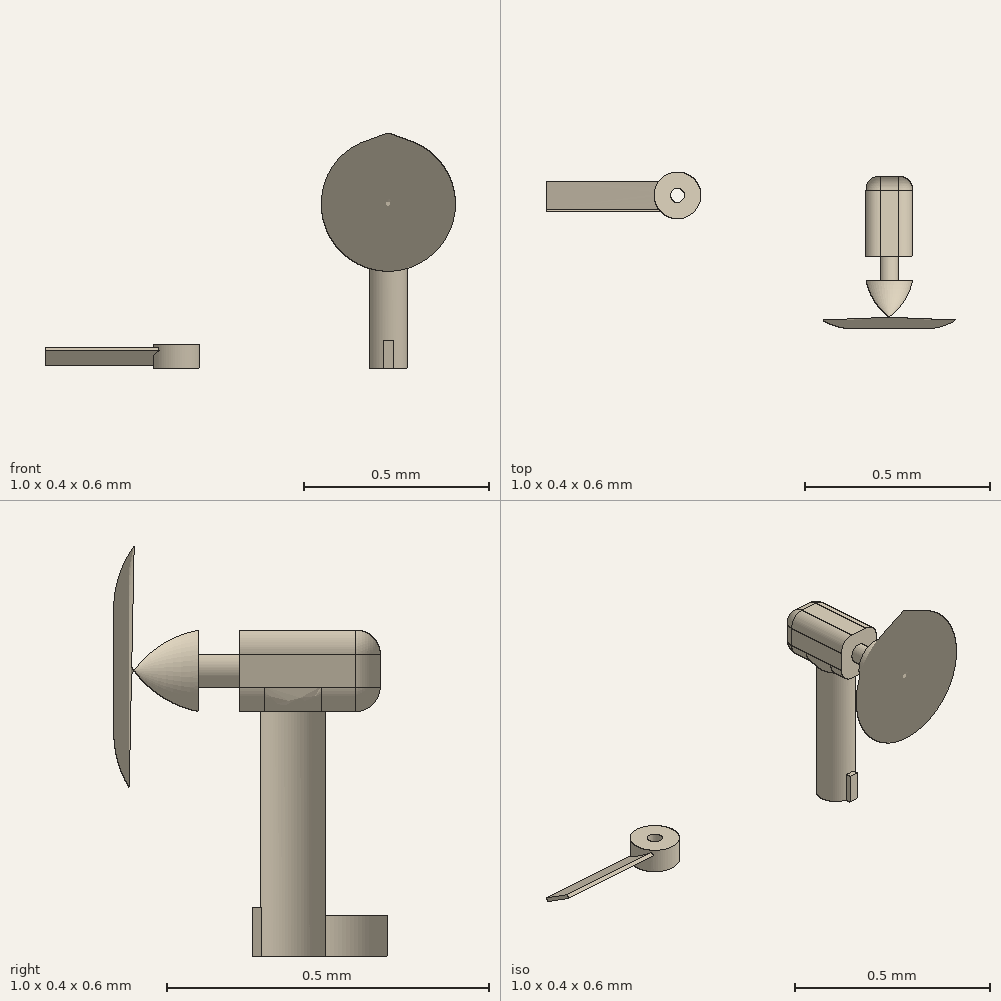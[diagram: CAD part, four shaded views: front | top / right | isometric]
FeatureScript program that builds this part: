
annotation { "Feature Type Name" : "Feature", "Feature Type Description" : "" }
export const myFeature = defineFeature(function(context is Context, id is Id, definition is map)
    precondition{}
    {
        {
            var Q0;
            Q0=qCreatedBy(makeId("Top.planeOp"),FACE);
            var sketch = newSketch(context, id + "F0", { "sketchPlane" : qUnion([Q0])});
            skCircle(sketch, "E0", {"center": v(0, 0) * mm, "radius": 0.05 * mm});
            skSolve(sketch);
        }
        {
            var Q0;
            Q0 = qSketchRegion(id + "F0", true);
            extrude(context, id + "F1", {"entities" : qUnion([Q0]), "depth" : 0.38 * mm});
        }
        {
            var Q0;
            Q0=makeQuery(id+"F1.opExtrude","CAP_FACE",FACE,{"disambiguationData":[OSD([sQuery(id+"F0.wireOp",EDGE,"E0")])],"isStart":false});
            var sketch = newSketch(context, id + "F2", { "sketchPlane" : qUnion([Q0])});
            skLineSegment(sketch, "E1.bottom", {"start": v(0.06, 0.14) * mm, "end": v(-0.06, 0.14) * mm});
            skLineSegment(sketch, "E1.left", {"start": v(0.06, 0.14) * mm, "end": v(0.06, -0.08) * mm});
            skLineSegment(sketch, "E1.right", {"start": v(-0.06, 0.14) * mm, "end": v(-0.06, -0.08) * mm});
            skPoint(sketch, "E1.middle", {"position": v(0, 0) * mm});
            skLineSegment(sketch, "E2", {"start": v(0.06, -0.08) * mm, "end": v(-0.06, -0.08) * mm});
            skPoint(sketch, "E1.top.end.orphan", {"position": v(-0.06, -0.14) * mm});
            skPoint(sketch, "E1.top.start.orphan", {"position": v(0.06, -0.14) * mm});
            skSolve(sketch);
        }
        {
            var Q0;
            Q0 = qSketchRegion(id + "F2", true);
            extrude(context, id + "F3", {"entities" : qUnion([Q0]), "operationType" : NewBodyOperationType.ADD, "depth" : 0.13 * mm});
        }
        {
            var Q0;
            Q0=makeQuery(id+"F3.opExtrude","CAP_EDGE",EDGE,{"disambiguationData":[OSD([sQuery(id+"F2.wireOp",EDGE,"E1.right")])],"isStart":false});
            var Q1;
            Q1=makeQuery(id+"F3.opExtrude","CAP_EDGE",EDGE,{"disambiguationData":[OSD([sQuery(id+"F2.wireOp",EDGE,"E1.right")])],"isStart":true});
            var Q2;
            Q2=makeQuery(id+"F3.opExtrude","CAP_EDGE",EDGE,{"disambiguationData":[OSD([sQuery(id+"F2.wireOp",EDGE,"E1.left")])],"isStart":true});
            var Q3;
            Q3=makeQuery(id+"F3.opExtrude","CAP_EDGE",EDGE,{"disambiguationData":[OSD([sQuery(id+"F2.wireOp",EDGE,"E1.left")])],"isStart":false});
            fillet(context, id + "F4", {"entities" : qUnion([Q0, Q1, Q2, Q3]), "radius" : 0.04 * mm, "tangentPropagation" : true, "allowEdgeOverflow" : false});
        }
        {
            var Q0;
            Q0=makeQuery(id+"F3.opExtrude","SWEPT_FACE",FACE,{"disambiguationData":[OSD([sQuery(id+"F2.wireOp",EDGE,"E2")])]});
            var sketch = newSketch(context, id + "F5", { "sketchPlane" : qUnion([Q0])});
            skLineSegment(sketch, "E3.0", {"start": v(0.03, 0.5) * mm, "end": v(-0.03, 0.5) * mm});
            skLineSegment(sketch, "E4.0", {"start": v(-0.06, 0.47) * mm, "end": v(-0.06, 0.42) * mm});
            skCircle(sketch, "E5", {"center": v(0, 0.44) * mm, "radius": 0.03 * mm});
            skPoint(sketch, "E5.centerSnap0", {"position": v(0, 0.5) * mm});
            skPoint(sketch, "E5.centerSnap1", {"position": v(-0.06, 0.44) * mm});
            skSolve(sketch);
        }
        {
            var Q0;
            Q0 = qSketchRegion(id + "F5", true);
            extrude(context, id + "F6", {"entities" : qUnion([Q0]), "operationType" : NewBodyOperationType.ADD, "depth" : 0.06 * mm});
        }
        {
            var Q0;
            Q0=makeQuery(id+"F3.opExtrude","CAP_EDGE",EDGE,{"disambiguationData":[OSD([sQuery(id+"F2.wireOp",EDGE,"E1.bottom")])],"isStart":false});
            var Q1;
            Q1=makeQuery(id+"F4.opFillet","BLEND_EDGE",EDGE,{"blendedFrom":[makeQuery(id+"F3.opExtrude","CAP_EDGE",EDGE,{"disambiguationData":[OSD([sQuery(id+"F2.wireOp",EDGE,"E1.right")])],"isStart":false}),makeQuery(id+"F3.opExtrude","SWEPT_FACE",FACE,{"disambiguationData":[OSD([sQuery(id+"F2.wireOp",EDGE,"E1.bottom")])]})],"blendedInto":[makeQuery(id+"F3.opExtrude","SWEPT_FACE",FACE,{"disambiguationData":[OSD([sQuery(id+"F2.wireOp",EDGE,"E1.bottom")])]})]});
            var Q2;
            Q2=makeQuery(id+"F3.opExtrude","SWEPT_EDGE",EDGE,{"disambiguationData":[OSD([sQuery(id+"F2.wireOp",EDGE,"E1.bottom"),sQuery(id+"F2.wireOp",EDGE,"E1.right")])]});
            var Q3;
            Q3=makeQuery(id+"F4.opFillet","BLEND_EDGE",EDGE,{"blendedFrom":[makeQuery(id+"F3.opExtrude","CAP_EDGE",EDGE,{"disambiguationData":[OSD([sQuery(id+"F2.wireOp",EDGE,"E1.right")])],"isStart":true}),makeQuery(id+"F3.opExtrude","SWEPT_FACE",FACE,{"disambiguationData":[OSD([sQuery(id+"F2.wireOp",EDGE,"E1.bottom")])]})],"blendedInto":[makeQuery(id+"F3.opExtrude","SWEPT_FACE",FACE,{"disambiguationData":[OSD([sQuery(id+"F2.wireOp",EDGE,"E1.bottom")])]})]});
            var Q4;
            Q4=makeQuery(id+"F3.opExtrude","CAP_EDGE",EDGE,{"disambiguationData":[OSD([sQuery(id+"F2.wireOp",EDGE,"E1.bottom")])],"isStart":true});
            var Q5;
            Q5=makeQuery(id+"F4.opFillet","BLEND_EDGE",EDGE,{"blendedFrom":[makeQuery(id+"F3.opExtrude","CAP_EDGE",EDGE,{"disambiguationData":[OSD([sQuery(id+"F2.wireOp",EDGE,"E1.left")])],"isStart":true}),makeQuery(id+"F3.opExtrude","SWEPT_FACE",FACE,{"disambiguationData":[OSD([sQuery(id+"F2.wireOp",EDGE,"E1.bottom")])]})],"blendedInto":[makeQuery(id+"F3.opExtrude","SWEPT_FACE",FACE,{"disambiguationData":[OSD([sQuery(id+"F2.wireOp",EDGE,"E1.bottom")])]})]});
            var Q6;
            Q6=makeQuery(id+"F3.opExtrude","SWEPT_EDGE",EDGE,{"disambiguationData":[OSD([sQuery(id+"F2.wireOp",EDGE,"E1.bottom"),sQuery(id+"F2.wireOp",EDGE,"E1.left")])]});
            var Q7;
            Q7=makeQuery(id+"F4.opFillet","BLEND_EDGE",EDGE,{"blendedFrom":[makeQuery(id+"F3.opExtrude","CAP_EDGE",EDGE,{"disambiguationData":[OSD([sQuery(id+"F2.wireOp",EDGE,"E1.left")])],"isStart":false}),makeQuery(id+"F3.opExtrude","SWEPT_FACE",FACE,{"disambiguationData":[OSD([sQuery(id+"F2.wireOp",EDGE,"E1.bottom")])]})],"blendedInto":[makeQuery(id+"F3.opExtrude","SWEPT_FACE",FACE,{"disambiguationData":[OSD([sQuery(id+"F2.wireOp",EDGE,"E1.bottom")])]})]});
            fillet(context, id + "F7", {"entities" : qUnion([Q0, Q1, Q2, Q3, Q4, Q5, Q6, Q7]), "radius" : 0.04 * mm, "tangentPropagation" : true, "allowEdgeOverflow" : false});
        }
        {
            var Q0;
            Q0=qCreatedBy(makeId("Right.planeOp"),FACE);
            var sketch = newSketch(context, id + "F8", { "sketchPlane" : qUnion([Q0])});
            skLineSegment(sketch, "E6.0", {"start": v(-0.08, 0.5) * mm, "end": v(0.1, 0.5) * mm});
            skLineSegment(sketch, "E7.0", {"start": v(-0.04, 0.38) * mm, "end": v(-0.08, 0.38) * mm});
            skLineSegment(sketch, "E8.0", {"start": v(-0.15, 0.42) * mm, "end": v(-0.15, 0.47) * mm});
            skLineSegment(sketch, "E9", {"start": v(-0.15, 0.47) * mm, "end": v(-0.15, 0.5) * mm});
            skLineSegment(sketch, "E10", {"start": v(-0.15, 0.42) * mm, "end": v(-0.15, 0.38) * mm});
            skLineSegment(sketch, "E11", {"start": v(-0.15, 0.44) * mm, "end": v(-0.25, 0.44) * mm});
            skArc(sketch, "E12", {"start": v(-0.15, 0.5) * mm, "mid": v(-0.2, 0.49) * mm, "end": v(-0.25, 0.44) * mm});
            skArc(sketch, "E13.MirrorCS", {"start": v(-0.15, 0.38) * mm, "mid": v(-0.2, 0.4) * mm, "end": v(-0.25, 0.44) * mm});
            skSolve(sketch);
        }
        {
            var Q0;
            {var subQ0=sQuery(id+"F8.wireOp",EDGE,"E9");Q0=makeQuery(id+"F8.imprint","IMPRINT",FACE,{"disambiguationData":[TD([[makeQuery(id+"F8.imprint","IMPRINT",EDGE,{"derivedFrom":subQ0}),1.0]])]});}
            var Q1;
            Q1=sQuery(id+"F8.wireOp",EDGE,"E11");
            revolve(context, id + "F9", {"operationType" : NewBodyOperationType.ADD, "entities" : qUnion([Q0]), "axis" : qUnion([Q1]), "revolveType" : RevolveType.FULL});
        }
        {
            var Q0;
            Q0=qCreatedBy(makeId("Top.planeOp"),FACE);
            var sketch = newSketch(context, id + "F10", { "sketchPlane" : qUnion([Q0])});
            skCircle(sketch, "E14", {"center": v(-0.57, 0.08) * mm, "radius": 0.06 * mm});
            skCircle(sketch, "E15", {"center": v(-0.57, 0.08) * mm, "radius": 0.02 * mm});
            skSolve(sketch);
        }
        {
            var Q0;
            Q0 = qSketchRegion(id + "F10", true);
            extrude(context, id + "F11", {"entities" : qUnion([Q0]), "depth" : 0.06 * mm});
        }
        {
            var Q0;
            Q0=makeQuery(id+"F11.opExtrude","SWEPT_FACE",FACE,{"disambiguationData":[OSD([sQuery(id+"F10.wireOp",EDGE,"E14")])]});
            cPlane(context, id + "F12", {"entities" : qUnion([Q0]), "cplaneType" : CPlaneType.LINE_ANGLE, "offset" : 25.4 * mm, "angle" : 0 * degree, "width" : 152.4 * mm, "height" : 152.4 * mm});
        }
        {
            var Q0;
            Q0=qCreatedBy(id+"F12.planeOp",FACE);
            cPlane(context, id + "F13", {"entities" : qUnion([Q0]), "cplaneType" : CPlaneType.OFFSET, "offset" : 0.36 * mm, "width" : 152.4 * mm, "height" : 152.4 * mm});
        }
        {
            var Q0;
            Q0=qCreatedBy(id+"F13.planeOp",FACE);
            var sketch = newSketch(context, id + "F14", { "sketchPlane" : qUnion([Q0])});
            skLineSegment(sketch, "E16.0", {"start": v(-0.15, 0.06) * mm, "end": v(-0.02, 0.06) * mm});
            skLineSegment(sketch, "E17.0", {"start": v(-0.15, 0) * mm, "end": v(-0.02, 0) * mm});
            skLineSegment(sketch, "E18", {"start": v(-0.12, 0.02) * mm, "end": v(-0.05, 0.06) * mm});
            skLineSegment(sketch, "E19", {"start": v(-0.05, 0.06) * mm, "end": v(-0.04, 0.05) * mm});
            skLineSegment(sketch, "E20", {"start": v(-0.04, 0.05) * mm, "end": v(-0.11, 0) * mm});
            skLineSegment(sketch, "E21", {"start": v(-0.12, 0.02) * mm, "end": v(-0.12, 0) * mm});
            skLineSegment(sketch, "E22", {"start": v(-0.11, 0) * mm, "end": v(-0.12, 0) * mm});
            skSolve(sketch);
        }
        {
            var Q0;
            Q0 = qSketchRegion(id + "F14", true);
            extrude(context, id + "F15", {"entities" : qUnion([Q0]), "operationType" : NewBodyOperationType.ADD, "endBound" : BoundingType.UP_TO_NEXT, "oppositeDirection" : true, "depth" : 25.4 * mm});
        }
        {
            var Q0;
            Q0=makeQuery(id+"F1.opExtrude","CAP_FACE",FACE,{"disambiguationData":[OSD([sQuery(id+"F0.wireOp",EDGE,"E0")])],"isStart":true});
            var sketch = newSketch(context, id + "F16", { "sketchPlane" : qUnion([Q0])});
            skPoint(sketch, "E23.0", {"position": v(0, 0) * mm});
            skCircle(sketch, "E24.0.0", {"center": v(0, 0) * mm, "radius": 0.05 * mm});
            skSolve(sketch);
        }
        {
            var Q0;
            Q0 = qSketchRegion(id + "F16", true);
            extrude(context, id + "F17", {"entities" : qUnion([Q0]), "operationType" : NewBodyOperationType.REMOVE, "oppositeDirection" : true, "depth" : 0.08 * mm});
        }
        {
            var Q0;
            Q0=makeQuery(id+"F17.boolean.opBoolean","COPY",FACE,{"derivedFrom":makeQuery(id+"F17.opExtrude","CAP_FACE",FACE,{"disambiguationData":[OSD([sQuery(id+"F16.wireOp",EDGE,"E24.0.0")])],"isStart":false})});
            var sketch = newSketch(context, id + "F18", { "sketchPlane" : qUnion([Q0])});
            skArc(sketch, "E25.0.0", {"start": v(-0.01, 0.05) * mm, "mid": v(0, -0.05) * mm, "end": v(0.01, 0.05) * mm});
            skLineSegment(sketch, "E26", {"start": v(0, 0) * mm, "end": v(0, 0.06) * mm});
            skLineSegment(sketch, "E27", {"start": v(0, 0.06) * mm, "end": v(-0.01, 0.06) * mm});
            skLineSegment(sketch, "E28.MirrorCS", {"start": v(0, 0.06) * mm, "end": v(0.01, 0.06) * mm});
            skLineSegment(sketch, "E29", {"start": v(-0.01, 0.06) * mm, "end": v(-0.01, 0.05) * mm});
            skLineSegment(sketch, "E30", {"start": v(0.01, 0.06) * mm, "end": v(0.01, 0.05) * mm});
            skSolve(sketch);
        }
        {
            var Q0;
            Q0 = qSketchRegion(id + "F18", true);
            extrude(context, id + "F19", {"entities" : qUnion([Q0]), "operationType" : NewBodyOperationType.ADD, "depth" : 0.08 * mm});
        }
    });
